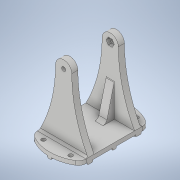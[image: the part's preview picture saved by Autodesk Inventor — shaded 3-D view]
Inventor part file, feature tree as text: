
AUTODESK INVENTOR PART (.ipt)
format: ipt  version: 2020 (Build 240168000, 168)  size: 373,248 bytes
history: native  units: in
note: dims shown in document units (in); Inventor stores cm internally (conversion verified against a paired STEP export)
features: extrude x9, sketch x9, fillet x6, pattern_circular x2, chamfer x2, mirror x1, projected_geometry x1
ambient origin geometry x8: Origin, YZ Plane, XZ Plane, XY Plane, X Axis, Y Axis, Z Axis, Center Point
bodies: Solid1 (feature_tree)
feature tree (30):
  extrude  "Extrusion1"  Depth=0.975in
  extrude  "Extrusion2"  Depth=0.125in TaperAngle=0.0deg
  pattern_circular  "Circular Pattern1"  Count=8 Angle=360.0deg
  extrude  "Extrusion3"  Depth=0.06in TaperAngle=0.0deg
  fillet  "Fillet1"  Radius=0.025in
  extrude  "Extrusion4"  TaperAngle=22.5deg  [1 undecoded]
  pattern_circular  "Circular Pattern2"  Count=8 Angle=360.0deg
  extrude  "Extrusion6"  Depth=0.75in
  extrude  "Extrusion7"  Depth=2.0in
  extrude  "Extrusion9"  Depth=0.125in
  fillet  "Fillet3"  Radius=1.625in
  extrude  "Extrusion10"  Depth=1.25in
  mirror  "Mirror1"
  fillet  "Fillet4"  Radius=1.25in
  chamfer  "Chamfer3"  Distance=2.5in
  chamfer  "Chamfer4"  Distance=1.5in
  sketch  "Sketch12"  dims[d31=0.5in d32=0.125in d33=1.625in d34=0.0in d35=2.0in d36=1.25in d37=2.5in d38=0.0in d50=1.5in d51=3.0in d52=0.5in d53=0.5in d54=2.5in d55=0.0in d56=0.25in d57=0.2165in d58=0.1in d59=0.0in d60=0.0625in d61=1.0in d62=0.25in d63=45.0deg d64=1.0in d65=0.25in d66=45.0deg d67=0.25in d70=0.125in d71=0.125in d72=0.125in d73=1.25in d74=2.0in d75=0.0in]
  fillet  "Fillet5"  Radius=3.0in
  fillet  "Fillet6"  Radius=0.5in
  fillet  "Fillet7"  Radius=0.5in
  extrude  "Extrusion12"  Depth=1.25in TaperAngle=0.0deg
  sketch  "Sketch1"  dims[d0=2.5in d1=0.975in]
  sketch  "Sketch2"  dims[d2=0.125in d3=0.0in d6=0.06in d7=0.0in d8=3.1496in d9=360.0deg]
  projected_geometry  "Projected Loop1"
  sketch  "Sketch3"  dims[d11=0.99in d12=0.06in d13=0.0in d14=0.025in]
  sketch  "Sketch4"  dims[d15=1.1in d16=22.5deg]
  sketch  "Sketch6"  dims[d17=0.125in]
  sketch  "Sketch7"  dims[d18=1.0in d19=0.0in d20=3.1496in d21=360.0deg]
  sketch  "Sketch10"  dims[d23=0.12in d28=0.75in]
  sketch  "Sketch11"  dims[d29=1.5in d30=2.0in]
note: 1 required parameter value undecoded (feature->parameter linkage not recoverable at this tier; creation-order binding heuristic only, values carry confidence <= 0.55)
